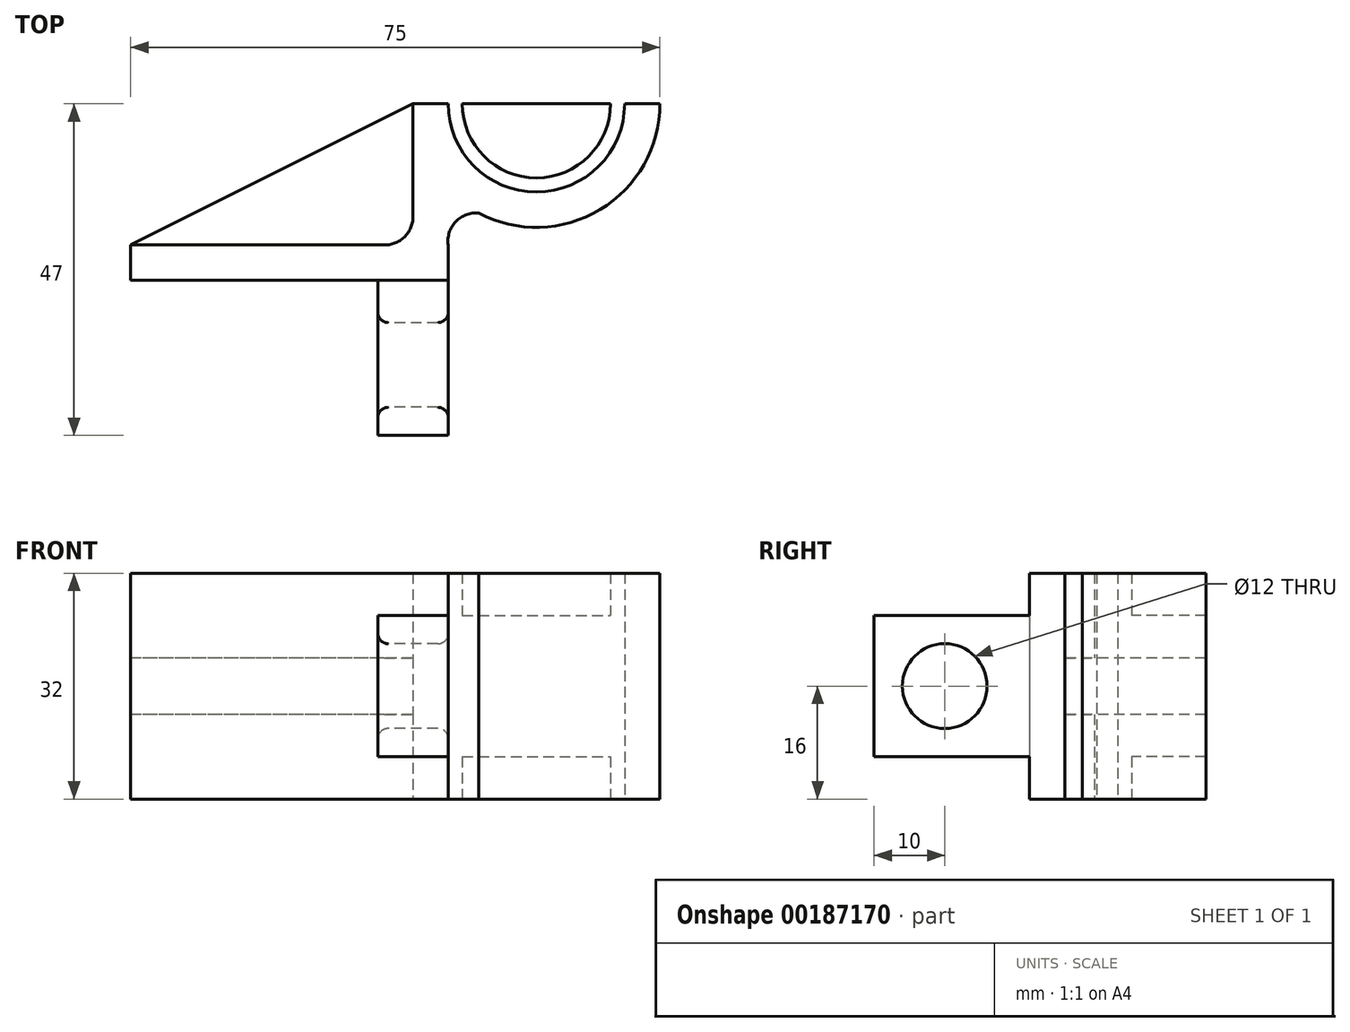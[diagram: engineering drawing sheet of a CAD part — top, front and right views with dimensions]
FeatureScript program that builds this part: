
annotation { "Feature Type Name" : "Feature", "Feature Type Description" : "" }
export const myFeature = defineFeature(function(context is Context, id is Id, definition is map)
    precondition{}
    {
        {
            var Q0;
            Q0=qCreatedBy(makeId("Top.planeOp"),FACE);
            var sketch = newSketch(context, id + "F0", { "sketchPlane" : qUnion([Q0])});
            skLineSegment(sketch, "E0", {"start": v(5.18, 5) * mm, "end": v(-30.83, 5) * mm});
            skLineSegment(sketch, "E1", {"start": v(-30.83, 5) * mm, "end": v(-30.83, 0) * mm});
            skLineSegment(sketch, "E2", {"start": v(-30.83, 5) * mm, "end": v(-30.83, 25) * mm});
            skArc(sketch, "E3", {"start": v(5.18, 5) * mm, "mid": v(8.08, 6.25) * mm, "end": v(9.18, 9.2) * mm});
            skLineSegment(sketch, "E4", {"start": v(9.17, 25) * mm, "end": v(9.18, 9.2) * mm});
            skPoint(sketch, "E5.orphan", {"position": v(14.17, 5) * mm});
            skLineSegment(sketch, "E6", {"start": v(9.17, 25) * mm, "end": v(-30.83, 5) * mm});
            skLineSegment(sketch, "E7", {"start": v(-30.83, 0) * mm, "end": v(14.2, 0) * mm});
            skLineSegment(sketch, "E8", {"start": v(5.18, 5) * mm, "end": v(14.17, 5) * mm});
            skPoint(sketch, "E9", {"position": v(14.17, 25) * mm});
            skArc(sketch, "E10", {"start": v(44.17, 25) * mm, "mid": v(35.7, 10) * mm, "end": v(18.49, 9.53) * mm});
            skLineSegment(sketch, "E11.trimOffspring", {"start": v(14.17, 25) * mm, "end": v(14.17, 25) * mm});
            skArc(sketch, "E12", {"start": v(18.49, 9.53) * mm, "mid": v(15.24, 8.3) * mm, "end": v(14.17, 5) * mm});
            skLineSegment(sketch, "E13", {"start": v(14.17, 5) * mm, "end": v(14.2, 0) * mm});
            skArc(sketch, "E14", {"start": v(37.17, 25) * mm, "mid": v(26.67, 14.5) * mm, "end": v(16.17, 25) * mm});
            skArc(sketch, "E15", {"start": v(39.17, 25) * mm, "mid": v(26.67, 12.5) * mm, "end": v(14.17, 25) * mm});
            skArc(sketch, "E16.trimOffspring", {"start": v(9.17, 24.98) * mm, "mid": v(9.17, 25) * mm, "end": v(9.17, 25) * mm});
            skLineSegment(sketch, "E17", {"start": v(14.17, 25) * mm, "end": v(9.17, 25) * mm});
            skLineSegment(sketch, "E18", {"start": v(14.17, 25) * mm, "end": v(44.17, 25) * mm});
            skLineSegment(sketch, "E19", {"start": v(9.17, 25) * mm, "end": v(-30.83, 25) * mm});
            skSolve(sketch);
        }
        {
            var Q0;
            Q0=makeQuery(id+"F0.imprint","IMPRINT",FACE,{"disambiguationData":[TD([[makeQuery(id+"F0.imprint","IMPRINT",EDGE,{"derivedFrom":sQuery(id+"F0.wireOp",EDGE,"E0")}),1.0]])]});
            var Q1;
            Q1=makeQuery(id+"F0.imprint","IMPRINT",FACE,{"disambiguationData":[TD([[makeQuery(id+"F0.imprint","IMPRINT",EDGE,{"derivedFrom":sQuery(id+"F0.wireOp",EDGE,"E3")}),-1.0]])]});
            var Q2;
            {var subQ0=sQuery(id+"F0.wireOp",EDGE,"E18");var subQ3=sQuery(id+"F0.wireOp",EDGE,"E14");var subQ7=makeQuery(id+"F0.imprint","INTERSECT",VERTEX,{"disambiguationData":[OD(0.0)],"derivedFrom":[subQ3,subQ0]});Q2=makeQuery(id+"F0.imprint","IMPRINT",FACE,{"disambiguationData":[TD([[makeQuery(id+"F0.imprint","IMPRINT",EDGE,{"disambiguationData":[TD([[subQ7,-1.0]])],"derivedFrom":subQ3}),1.0]])]});}
            extrude(context, id + "F1", {"entities" : qUnion([Q0, Q1, Q2]), "endBound" : BoundingType.SYMMETRIC, "depth" : 32 * mm});
        }
        {
            var Q0;
            {var subQ1=sQuery(id+"F0.wireOp",EDGE,"E0");Q0=makeQuery(id+"F0.imprint","IMPRINT",FACE,{"disambiguationData":[TD([[makeQuery(id+"F0.imprint","IMPRINT",EDGE,{"derivedFrom":subQ1}),-1.0]])]});}
            extrude(context, id + "F2", {"entities" : qUnion([Q0]), "operationType" : NewBodyOperationType.ADD, "endBound" : BoundingType.SYMMETRIC, "depth" : 8 * mm});
        }
        {
            var Q0;
            {var subQ0=sQuery(id+"F0.wireOp",EDGE,"E18");var subQ3=sQuery(id+"F0.wireOp",EDGE,"E14");var subQ7=makeQuery(id+"F0.imprint","INTERSECT",VERTEX,{"disambiguationData":[OD(0.0)],"derivedFrom":[subQ3,subQ0]});Q0=makeQuery(id+"F0.imprint","IMPRINT",FACE,{"disambiguationData":[TD([[makeQuery(id+"F0.imprint","IMPRINT",EDGE,{"disambiguationData":[TD([[subQ7,-1.0]])],"derivedFrom":subQ3}),1.0]])]});}
            extrude(context, id + "F3", {"entities" : qUnion([Q0]), "operationType" : NewBodyOperationType.REMOVE, "endBound" : BoundingType.SYMMETRIC, "oppositeDirection" : true, "depth" : 20 * mm});
        }
        {
            var Q0;
            Q0=makeQuery(id+"F1.opExtrude","SWEPT_FACE",FACE,{"disambiguationData":[OSD([sQuery(id+"F0.wireOp",EDGE,"E7")])]});
            var sketch = newSketch(context, id + "F4", { "sketchPlane" : qUnion([Q0])});
            skLineSegment(sketch, "E20", {"start": v(-30.83, 16) * mm, "end": v(-30.83, -16) * mm});
            skPoint(sketch, "E21", {"position": v(-30.83, 0) * mm});
            skLineSegment(sketch, "E22", {"start": v(-30.83, 0) * mm, "end": v(-30.83, 10) * mm});
            skLineSegment(sketch, "E23", {"start": v(-30.83, 0) * mm, "end": v(-30.83, -10) * mm});
            skLineSegment(sketch, "E24", {"start": v(-30.83, 10) * mm, "end": v(-20.83, 10) * mm});
            skLineSegment(sketch, "E25", {"start": v(-20.83, 10) * mm, "end": v(-20.83, -10) * mm});
            skLineSegment(sketch, "E26", {"start": v(-20.83, -10) * mm, "end": v(-30.83, -10) * mm});
            skLineSegment(sketch, "E27", {"start": v(-30.83, -10) * mm, "end": v(14.2, -10) * mm});
            skPoint(sketch, "E28.endSnap0", {"position": v(-25.83, 10) * mm});
            skLineSegment(sketch, "E29", {"start": v(4.2, 10) * mm, "end": v(4.2, -10) * mm});
            skLineSegment(sketch, "E30.trimOffspring", {"start": v(4.2, 10) * mm, "end": v(14.2, 10) * mm});
            skSolve(sketch);
        }
        {
            var Q0;
            {var subQ3=sQuery(id+"F4.wireOp",EDGE,"E29");Q0=makeQuery(id+"F4.imprint","IMPRINT",FACE,{"disambiguationData":[TD([[makeQuery(id+"F4.imprint","IMPRINT",EDGE,{"derivedFrom":subQ3}),1.0]])]});}
            var Q1;
            Q1=makeQuery(id+"F4.imprint","IMPRINT",FACE,{"disambiguationData":[TD([[makeQuery(id+"F4.imprint","IMPRINT",EDGE,{"derivedFrom":sQuery(id+"F4.wireOp",EDGE,"E22")}),1.0]])]});
            extrude(context, id + "F5", {"entities" : qUnion([Q0, Q1]), "operationType" : NewBodyOperationType.ADD, "depth" : 22 * mm});
        }
        {
            var Q0;
            Q0=makeQuery(id+"F5.boolean.opBoolean","MERGE",FACE,{"derivedFrom":[makeQuery(id+"F1.opExtrude","SWEPT_FACE",FACE,{"disambiguationData":[OSD([sQuery(id+"F0.wireOp",EDGE,"E1")])]}),makeQuery(id+"F5.opExtrude","SWEPT_FACE",FACE,{"disambiguationData":[OSD([sQuery(id+"F4.wireOp",EDGE,"E22"),sQuery(id+"F4.wireOp",EDGE,"E23")])]})]});
            var sketch = newSketch(context, id + "F6", { "sketchPlane" : qUnion([Q0])});
            skPoint(sketch, "E31", {"position": v(12, 0) * mm});
            skArc(sketch, "E32", {"start": v(12, 10) * mm, "mid": v(22, 0) * mm, "end": v(12, -10) * mm});
            skCircle(sketch, "E33", {"center": v(12, 0) * mm, "radius": 6 * mm});
            skSolve(sketch);
        }
        {
            var Q0;
            {var subQ0=sQuery(id+"F6.wireOp",EDGE,"E32");var subQ1=sQuery(id+"F4.wireOp",EDGE,"E22");var subQ4=makeQuery(id+"F5.opExtrude","CAP_EDGE",EDGE,{"disambiguationData":[OSD([subQ1,sQuery(id+"F4.wireOp",EDGE,"E23")])],"isStart":false});var subQ5=makeQuery(id+"F6.imprint","INTERSECT",VERTEX,{"derivedFrom":[subQ4,subQ0]});Q0=makeQuery(id+"F6.imprint","IMPRINT",FACE,{"disambiguationData":[TD([[makeQuery(id+"F6.imprint","IMPRINT",EDGE,{"disambiguationData":[TD([[subQ5,1.0]])],"derivedFrom":subQ0}),1.0]])]});}
            var Q1;
            {var subQ0=sQuery(id+"F6.wireOp",EDGE,"E32");var subQ1=sQuery(id+"F4.wireOp",EDGE,"E23");var subQ4=makeQuery(id+"F5.opExtrude","CAP_EDGE",EDGE,{"disambiguationData":[OSD([sQuery(id+"F4.wireOp",EDGE,"E22"),subQ1])],"isStart":false});var subQ5=makeQuery(id+"F6.imprint","INTERSECT",VERTEX,{"derivedFrom":[subQ4,subQ0]});Q1=makeQuery(id+"F6.imprint","IMPRINT",FACE,{"disambiguationData":[TD([[makeQuery(id+"F6.imprint","IMPRINT",EDGE,{"disambiguationData":[TD([[subQ5,-1.0]])],"derivedFrom":subQ0}),1.0]])]});}
            var Q2;
            Q2=makeQuery(id+"F6.imprint","IMPRINT",FACE,{"disambiguationData":[TD([[makeQuery(id+"F6.imprint","IMPRINT",EDGE,{"derivedFrom":sQuery(id+"F6.wireOp",EDGE,"E33")}),1.0]])]});
            extrude(context, id + "F7", {"entities" : qUnion([Q0, Q1, Q2]), "operationType" : NewBodyOperationType.REMOVE, "endBound" : BoundingType.THROUGH_ALL, "oppositeDirection" : true, "depth" : 25 * mm});
        }
        {
            var Q0;
            Q0=makeQuery(id+"F7.boolean.opBoolean","COPY",EDGE,{"derivedFrom":makeQuery(id+"F7.opExtrude","CAP_EDGE",EDGE,{"disambiguationData":[OSD([sQuery(id+"F6.wireOp",EDGE,"E33")])],"isStart":true})});
            var Q1;
            Q1=makeQuery(id+"F7.boolean.opBoolean","INTERSECT",EDGE,{"derivedFrom":[makeQuery(id+"F5.opExtrude","SWEPT_FACE",FACE,{"disambiguationData":[OSD([sQuery(id+"F4.wireOp",EDGE,"E25")])]}),makeQuery(id+"F7.opExtrude","SWEPT_FACE",FACE,{"disambiguationData":[OSD([sQuery(id+"F6.wireOp",EDGE,"E33")])]})]});
            var Q2;
            Q2=makeQuery(id+"F7.boolean.opBoolean","INTERSECT",EDGE,{"derivedFrom":[makeQuery(id+"F5.opExtrude","SWEPT_FACE",FACE,{"disambiguationData":[OSD([sQuery(id+"F0.wireOp",EDGE,"E7"),sQuery(id+"F0.wireOp",EDGE,"E13")])]}),makeQuery(id+"F7.opExtrude","SWEPT_FACE",FACE,{"disambiguationData":[OSD([sQuery(id+"F6.wireOp",EDGE,"E33")])]})]});
            var Q3;
            Q3=makeQuery(id+"F7.boolean.opBoolean","INTERSECT",EDGE,{"derivedFrom":[makeQuery(id+"F5.opExtrude","SWEPT_FACE",FACE,{"disambiguationData":[OSD([sQuery(id+"F4.wireOp",EDGE,"E29")])]}),makeQuery(id+"F7.opExtrude","SWEPT_FACE",FACE,{"disambiguationData":[OSD([sQuery(id+"F6.wireOp",EDGE,"E33")])]})]});
            fillet(context, id + "F8", {"entities" : qUnion([Q0, Q1, Q2, Q3]), "radius" : 1.5 * mm, "allowEdgeOverflow" : false});
        }
    });
